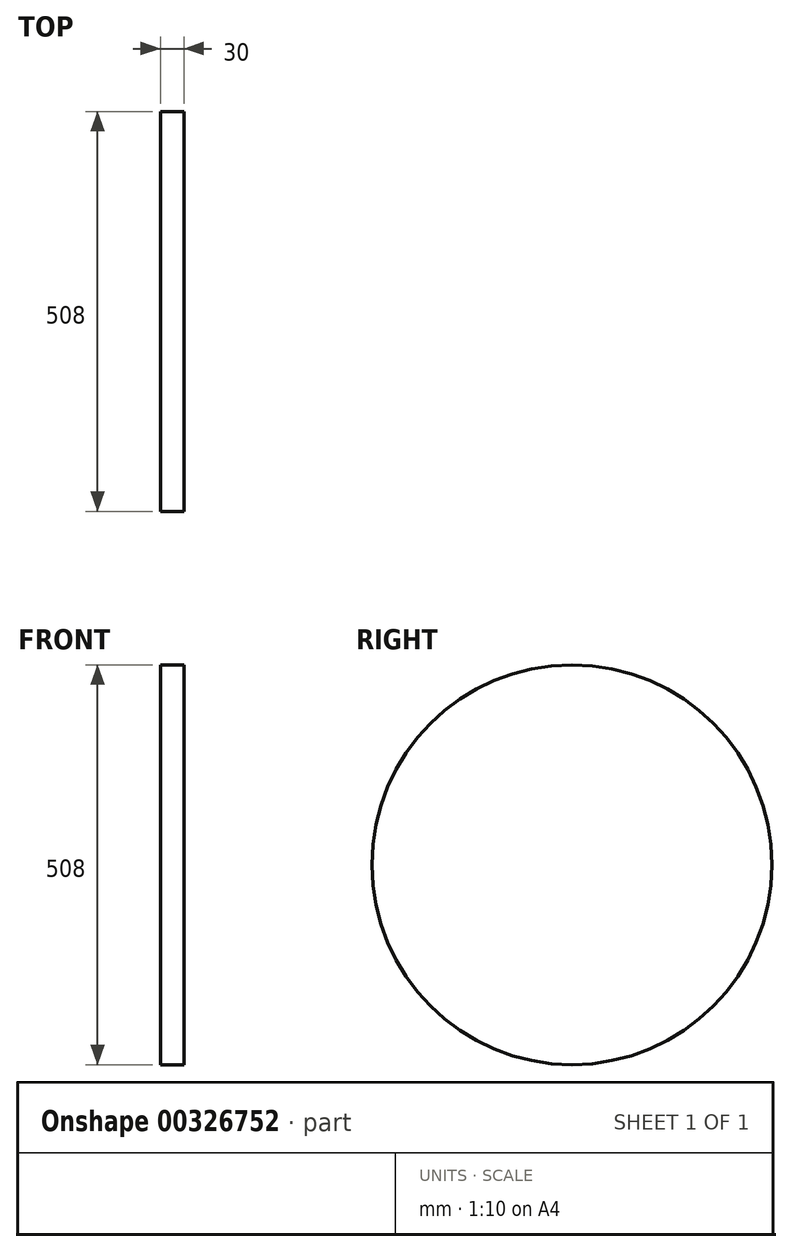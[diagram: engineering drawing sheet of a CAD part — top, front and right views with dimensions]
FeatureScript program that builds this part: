
annotation { "Feature Type Name" : "Feature", "Feature Type Description" : "" }
export const myFeature = defineFeature(function(context is Context, id is Id, definition is map)
    precondition{}
    {
        {
            var Q0;
            Q0=qCreatedBy(makeId("Right.planeOp"),FACE);
            var sketch = newSketch(context, id + "F0", { "sketchPlane" : qUnion([Q0])});
            skCircle(sketch, "E0", {"center": v(25.66, 52.06) * mm, "radius": 254 * mm});
            skSolve(sketch);
        }
        {
            var Q0;
            Q0 = qSketchRegion(id + "F0", true);
            extrude(context, id + "F1", {"entities" : qUnion([Q0]), "depth" : 30 * mm});
        }
    });
